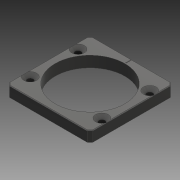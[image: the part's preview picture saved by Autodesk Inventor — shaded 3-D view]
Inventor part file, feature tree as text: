
AUTODESK INVENTOR PART (.ipt)
format: ipt  version: 2023 (Build 270158000, 158)  size: 182,272 bytes
history: native  units: mm
features: other x1, extrude x1, sketch x1, imported_body x1
ambient origin geometry x8: Origin, YZ Plane, XZ Plane, XY Plane, X Axis, Y Axis, Z Axis, Center Point
bodies: Body1 (feature_tree)
feature tree (4):
  other  "ソリッド1"
  extrude  "押し出し1"  TaperAngle=0.0deg  [1 undecoded]
  sketch  "スケッチ1"
  imported_body  "Base1"
note: 1 required parameter value undecoded (feature->parameter linkage not recoverable at this tier; creation-order binding heuristic only, values carry confidence <= 0.55)
